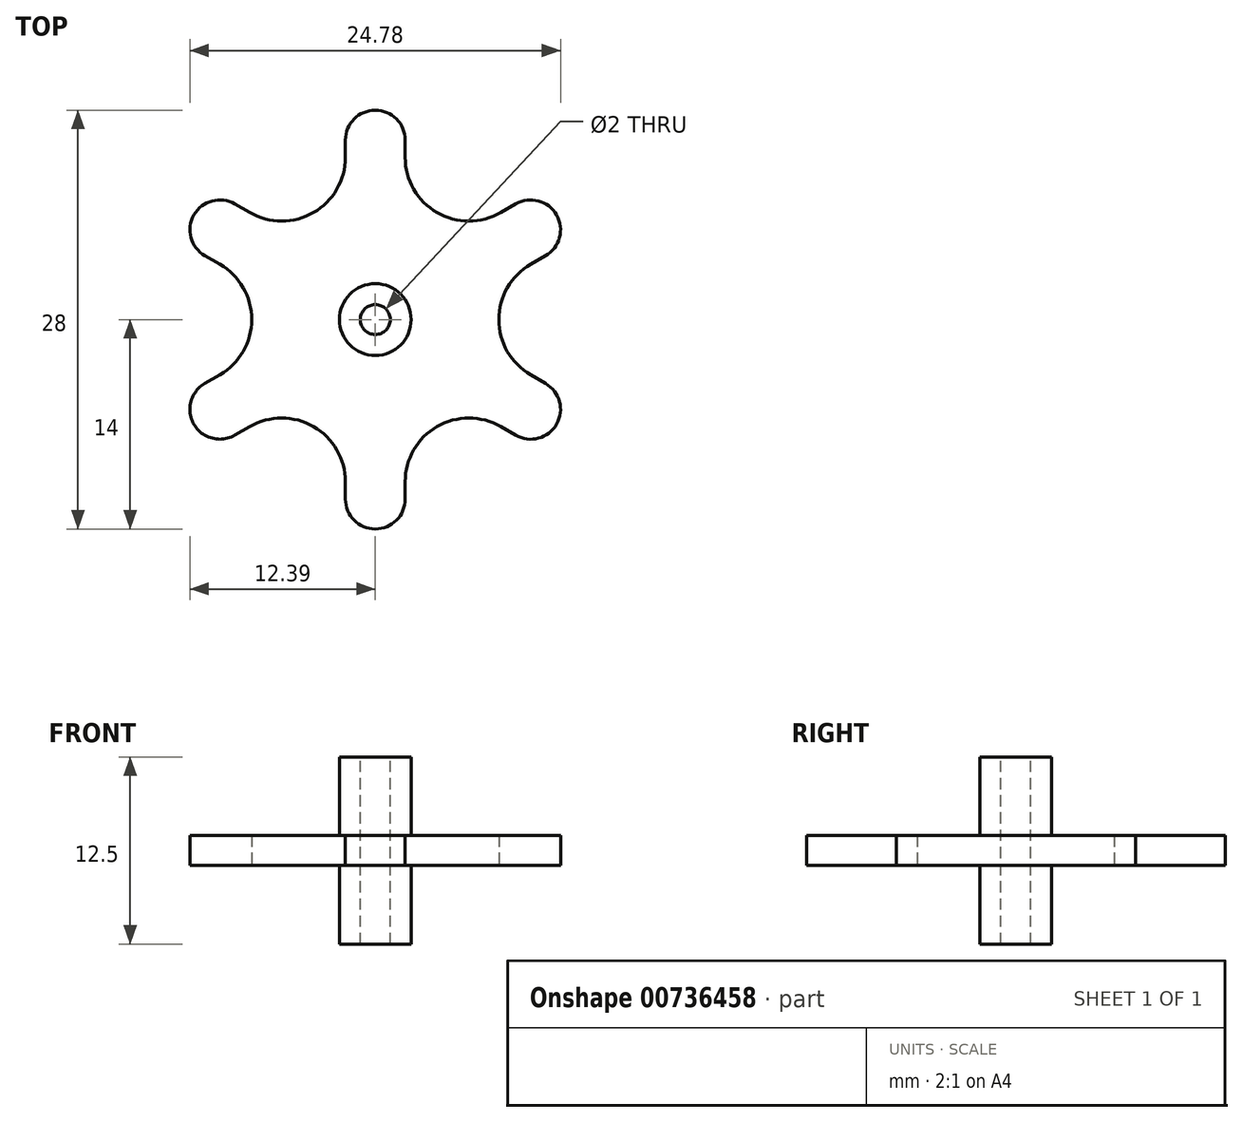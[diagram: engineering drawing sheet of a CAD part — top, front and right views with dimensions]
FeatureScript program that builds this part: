
annotation { "Feature Type Name" : "Feature", "Feature Type Description" : "" }
export const myFeature = defineFeature(function(context is Context, id is Id, definition is map)
    precondition{}
    {
        {
            var Q0;
            Q0=qCreatedBy(makeId("Top.planeOp"),FACE);
            var sketch = newSketch(context, id + "F0", { "sketchPlane" : qUnion([Q0])});
            skCircle(sketch, "E0.cCircle", {"center": v(0, 0) * mm, "radius": 12 * mm, "construction": true});
            skLineSegment(sketch, "E0.0", {"start": v(0, 12) * mm, "end": v(10.4, 6) * mm, "construction": true});
            skLineSegment(sketch, "E0.1", {"start": v(10.4, 6) * mm, "end": v(10.4, -6) * mm, "construction": true});
            skLineSegment(sketch, "E0.2", {"start": v(10.4, -6) * mm, "end": v(0, -12) * mm, "construction": true});
            skLineSegment(sketch, "E0.3", {"start": v(0, -12) * mm, "end": v(-10.4, -6) * mm, "construction": true});
            skLineSegment(sketch, "E0.4", {"start": v(-10.4, -6) * mm, "end": v(-10.4, 6) * mm, "construction": true});
            skLineSegment(sketch, "E0.5", {"start": v(-10.4, 6) * mm, "end": v(0, 12) * mm, "construction": true});
            skArc(sketch, "E1", {"start": v(2, 12) * mm, "mid": v(0, 14) * mm, "end": v(-2, 12) * mm});
            skLineSegment(sketch, "E2", {"start": v(2, 12) * mm, "end": v(2, 10.85) * mm});
            skLineSegment(sketch, "E3", {"start": v(-2, 12) * mm, "end": v(-2, 10.85) * mm});
            skLineSegment(sketch, "E4", {"start": v(-5.2, 9) * mm, "end": v(-4.13, 7.15) * mm, "construction": true});
            skArc(sketch, "E5", {"start": v(-4.13, 7.15) * mm, "mid": v(-2.57, 8.71) * mm, "end": v(-2, 10.85) * mm});
            skLineSegment(sketch, "E6", {"start": v(-4.13, 7.15) * mm, "end": v(-3, 7.81) * mm, "construction": true});
            skLineSegment(sketch, "E7", {"start": v(5.2, 9) * mm, "end": v(4.13, 7.15) * mm, "construction": true});
            skLineSegment(sketch, "E8", {"start": v(4.13, 7.15) * mm, "end": v(3, 7.81) * mm, "construction": true});
            skArc(sketch, "E9", {"start": v(2, 10.85) * mm, "mid": v(2.57, 8.71) * mm, "end": v(4.13, 7.15) * mm});
            skLineSegment(sketch, "E10", {"start": v(4.13, 7.15) * mm, "end": v(0, 0) * mm});
            skLineSegment(sketch, "E11", {"start": v(0, 0) * mm, "end": v(-4.13, 7.15) * mm});
            skSolve(sketch);
        }
        {
            var Q0;
            Q0 = qSketchRegion(id + "F0", true);
            extrude(context, id + "F1", {"entities" : qUnion([Q0]), "endBound" : BoundingType.SYMMETRIC, "depth" : 2 * mm, "offsetDistance" : 25 * mm});
        }
        {
            var Q0;
            Q0=makeQuery(id+"F1.opExtrude","SWEPT_BODY",BODY,{"disambiguationData":[OSD([sQuery(id+"F0.wireOp",EDGE,"E1"),sQuery(id+"F0.wireOp",EDGE,"E2"),sQuery(id+"F0.wireOp",EDGE,"E3"),sQuery(id+"F0.wireOp",EDGE,"E5"),sQuery(id+"F0.wireOp",EDGE,"E9"),sQuery(id+"F0.wireOp",EDGE,"E10"),sQuery(id+"F0.wireOp",EDGE,"E11")])]});
            var Q1;
            Q1=makeQuery(id+"F1.opExtrude","SWEPT_EDGE",EDGE,{"disambiguationData":[OSD([sQuery(id+"F0.wireOp",EDGE,"E10"),sQuery(id+"F0.wireOp",EDGE,"E11")])]});
            circularPattern(context, id + "F2", {"operationType" : NewBodyOperationType.ADD, "entities" : qUnion([Q0]), "axis" : qUnion([Q1]), "angle" : 360 * degree, "instanceCount" : 6, "equalSpace" : true});
        }
        {
            var Q0;
            Q0=qCreatedBy(makeId("Top.planeOp"),FACE);
            var sketch = newSketch(context, id + "F3", { "sketchPlane" : qUnion([Q0])});
            skCircle(sketch, "E12", {"center": v(0, 0) * mm, "radius": 2.4 * mm});
            skSolve(sketch);
        }
        {
            var Q0;
            Q0 = qSketchRegion(id + "F3", true);
            extrude(context, id + "F4", {"entities" : qUnion([Q0]), "operationType" : NewBodyOperationType.ADD, "endBound" : BoundingType.SYMMETRIC, "depth" : 12.5 * mm, "offsetDistance" : 25 * mm});
        }
        {
            var Q0;
            Q0=makeQuery(id+"F4.opExtrude","CAP_FACE",FACE,{"disambiguationData":[OSD([sQuery(id+"F3.wireOp",EDGE,"E12")])],"isStart":false});
            var sketch = newSketch(context, id + "F5", { "sketchPlane" : qUnion([Q0])});
            skCircle(sketch, "E13", {"center": v(0, 0) * mm, "radius": 1 * mm});
            skSolve(sketch);
        }
        {
            var Q0;
            Q0 = qSketchRegion(id + "F5", true);
            extrude(context, id + "F6", {"entities" : qUnion([Q0]), "operationType" : NewBodyOperationType.REMOVE, "endBound" : BoundingType.THROUGH_ALL, "oppositeDirection" : true, "depth" : 25 * mm, "offsetDistance" : 25 * mm});
        }
    });
